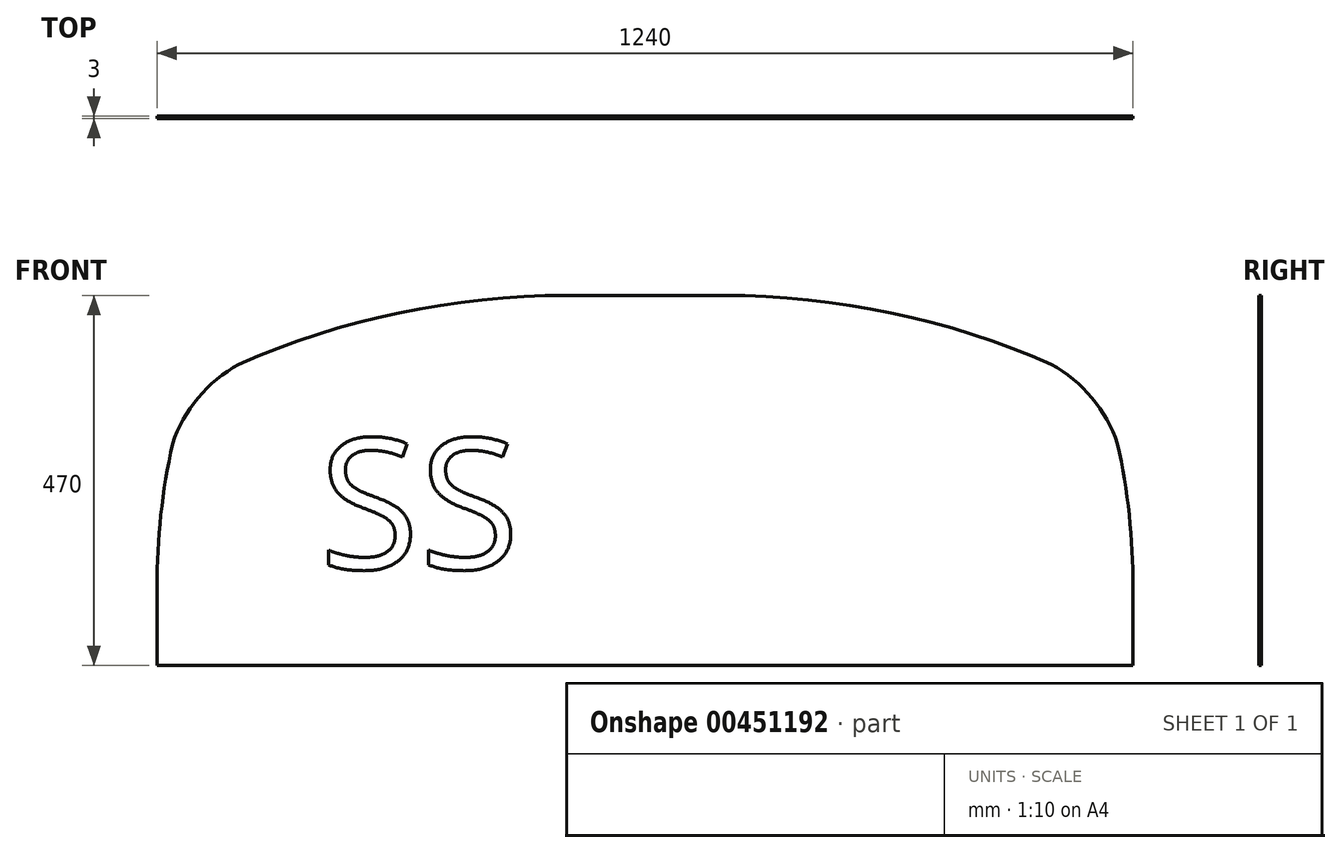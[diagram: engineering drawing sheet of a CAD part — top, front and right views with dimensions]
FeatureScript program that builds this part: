
annotation { "Feature Type Name" : "Feature", "Feature Type Description" : "" }
export const myFeature = defineFeature(function(context is Context, id is Id, definition is map)
    precondition{}
    {
        {
            var Q0;
            Q0=qCreatedBy(makeId("Front.planeOp"),FACE);
            var sketch = newSketch(context, id + "F0", { "sketchPlane" : qUnion([Q0])});
            skLineSegment(sketch, "E0", {"start": v(0, 0) * mm, "end": v(620, 0) * mm});
            skLineSegment(sketch, "E1", {"start": v(0, 0) * mm, "end": v(0, 470) * mm, "construction": true});
            skLineSegment(sketch, "E2", {"start": v(620, 0) * mm, "end": v(620, 100) * mm});
            skPoint(sketch, "E3", {"position": v(600.22, 281.66) * mm});
            skLineSegment(sketch, "E4", {"start": v(0, 470) * mm, "end": v(100, 470) * mm});
            skArc(sketch, "E5", {"start": v(620, 100) * mm, "mid": v(615.04, 191.37) * mm, "end": v(600.22, 281.66) * mm});
            skPoint(sketch, "E6", {"position": v(516.17, 382.63) * mm});
            skArc(sketch, "E7", {"start": v(516.17, 382.63) * mm, "mid": v(312.62, 447.92) * mm, "end": v(100, 470) * mm});
            skArc(sketch, "E8", {"start": v(600.22, 281.66) * mm, "mid": v(567.56, 339.94) * mm, "end": v(516.17, 382.63) * mm});
            skLineSegment(sketch, "E9.MirrorCS", {"start": v(-620, 0) * mm, "end": v(-620, 100) * mm});
            skPoint(sketch, "E10.MirrorP", {"position": v(-516.17, 382.63) * mm});
            skArc(sketch, "E11.MirrorCS", {"start": v(-620, 100) * mm, "mid": v(-615.04, 191.37) * mm, "end": v(-600.22, 281.66) * mm});
            skLineSegment(sketch, "E12.MirrorCS", {"start": v(0, 0) * mm, "end": v(-620, 0) * mm});
            skLineSegment(sketch, "E13.MirrorCS", {"start": v(0, 470) * mm, "end": v(-100, 470) * mm});
            skPoint(sketch, "E14.MirrorP", {"position": v(-600.22, 281.66) * mm});
            skArc(sketch, "E15.MirrorCS", {"start": v(-516.17, 382.63) * mm, "mid": v(-312.62, 447.92) * mm, "end": v(-100, 470) * mm});
            skArc(sketch, "E16.MirrorCS", {"start": v(-600.22, 281.66) * mm, "mid": v(-567.56, 339.94) * mm, "end": v(-516.17, 382.63) * mm});
            skSolve(sketch);
        }
        {
            var Q0;
            Q0 = qSketchRegion(id + "F0", true);
            extrude(context, id + "F1", {"entities" : qUnion([Q0]), "depth" : 3 * mm, "offsetDistance" : 25 * mm});
        }
        {
            var Q0;
            Q0=makeQuery(id+"F1.opExtrude","CAP_FACE",FACE,{"disambiguationData":[OSD([sQuery(id+"F0.wireOp",EDGE,"E0"),sQuery(id+"F0.wireOp",EDGE,"E2"),sQuery(id+"F0.wireOp",EDGE,"E4"),sQuery(id+"F0.wireOp",EDGE,"E5"),sQuery(id+"F0.wireOp",EDGE,"E7"),sQuery(id+"F0.wireOp",EDGE,"E8"),sQuery(id+"F0.wireOp",EDGE,"E9.MirrorCS"),sQuery(id+"F0.wireOp",EDGE,"E11.MirrorCS"),sQuery(id+"F0.wireOp",EDGE,"E12.MirrorCS"),sQuery(id+"F0.wireOp",EDGE,"E13.MirrorCS"),sQuery(id+"F0.wireOp",EDGE,"E15.MirrorCS"),sQuery(id+"F0.wireOp",EDGE,"E16.MirrorCS")])],"isStart":false});
            var sketch = newSketch(context, id + "F2", { "sketchPlane" : qUnion([Q0])});
            skText(sketch, "E17", { "text": "SS", "fontName": "OpenSans-Regular.ttf"});
            const initialGuessF2  = {"E17": [-0.41412, 0.1227, 1, 0, 0.16695]};
            skSetInitialGuess(sketch, initialGuessF2);
            skSolve(sketch);
        }
        {
            var Q0;
            Q0 = qSketchRegion(id + "F2", true);
            extrude(context, id + "F3", {"entities" : qUnion([Q0]), "operationType" : NewBodyOperationType.REMOVE, "oppositeDirection" : true, "depth" : 2 * mm, "offsetDistance" : 25 * mm});
        }
    });
